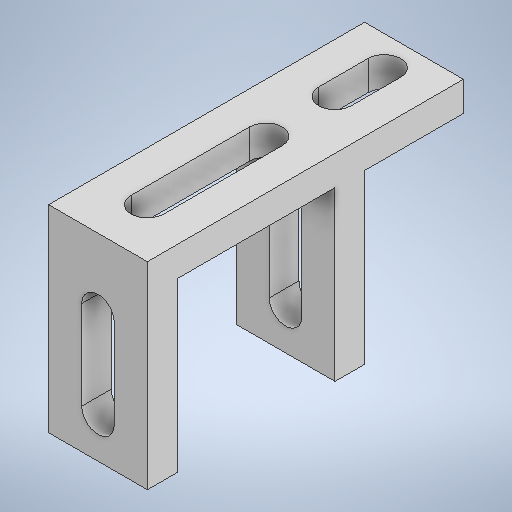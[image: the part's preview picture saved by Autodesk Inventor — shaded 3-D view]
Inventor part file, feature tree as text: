
AUTODESK INVENTOR PART (.ipt)
format: ipt  version: 2025.2 (Build 292293000, 293)  size: 263,680 bytes
history: native  units: mm
features: extrude x3, sketch x3
ambient origin geometry x8: Origin, YZ Plane, XZ Plane, XY Plane, X Axis, Y Axis, Z Axis, Center Point
bodies: Solid1 (feature_tree)
feature tree (6):
  extrude  "Extrusion1"  Depth=22.0mm
  extrude  "Extrusion2"  Depth=16.0mm
  extrude  "Extrusion3"  Depth=10.0mm
  sketch  "Sketch1"  dims[d0=20.0mm d1=22.0mm]
  sketch  "Sketch2"  dims[d2=14.0mm d3=16.0mm]
  sketch  "Sketch3"  dims[d4=3.0mm d5=10.0mm d6=10.0mm d7=0.0mm d8=2.0mm d9=2.0mm d10=3.3mm d11=2.0mm d12=3.0mm d13=3.3mm d14=0.0mm d15=0.0mm d16=4.0mm d17=4.0mm d18=3.3mm d19=0.0mm d20=0.0mm]
